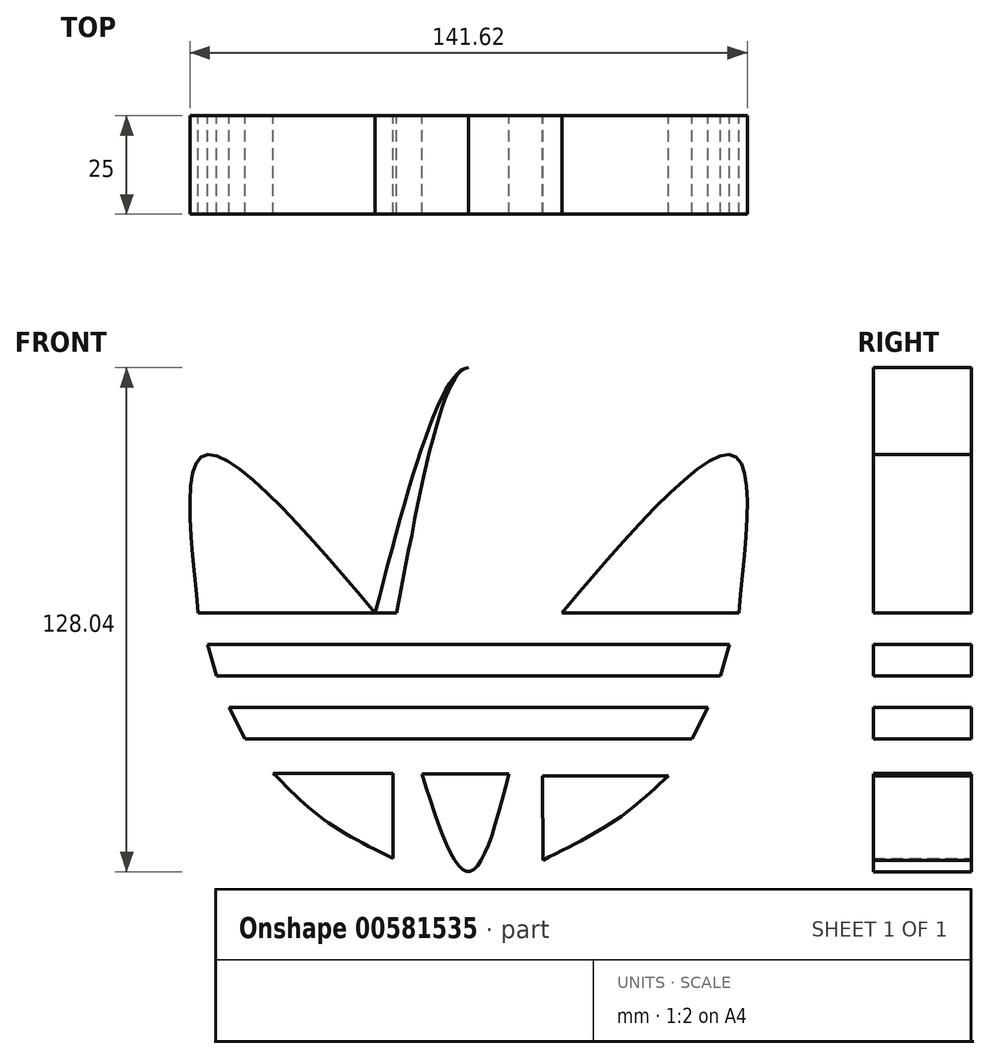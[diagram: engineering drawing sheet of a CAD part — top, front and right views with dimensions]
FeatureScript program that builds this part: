
annotation { "Feature Type Name" : "Feature", "Feature Type Description" : "" }
export const myFeature = defineFeature(function(context is Context, id is Id, definition is map)
    precondition{}
    {
        {
            var Q0;
            Q0=qCreatedBy(makeId("Front.planeOp"),FACE);
            var sketch = newSketch(context, id + "F0", { "sketchPlane" : qUnion([Q0])});
            skPoint(sketch, "E0", {"position": v(-0.15, -17.66) * mm});
            skLineSegment(sketch, "E1", {"start": v(-23.7, 0) * mm, "end": v(-68.7, 0) * mm});
            skFitSpline(sketch, "E2", {"points": [v(-23.7, 0) * mm, v(-67.37, 40) * mm, v(-68.7, 0) * mm], "startDerivative": vector(-83.92, 99.82) * mm, "endDerivative": vector(8.52, -106.38) * mm});
            skLineSegment(sketch, "E3", {"start": v(-23.7, 0) * mm, "end": v(0, 0) * mm});
            skFitSpline(sketch, "E4", {"points": [v(-23.7, 0) * mm, v(0, 62.34) * mm, v(18.3, 0) * mm], "startDerivative": vector(47.26, 186.76) * mm, "endDerivative": vector(36.72, -187.32) * mm});
            skLineSegment(sketch, "E5", {"start": v(-66.3, -8) * mm, "end": v(0, -8) * mm});
            skLineSegment(sketch, "E6", {"start": v(0, -16) * mm, "end": v(-63.96, -16) * mm});
            skLineSegment(sketch, "E7", {"start": v(-63.96, -16) * mm, "end": v(-66.3, -8) * mm});
            skLineSegment(sketch, "E8", {"start": v(-60.81, -24) * mm, "end": v(0, -24) * mm});
            skLineSegment(sketch, "E9", {"start": v(0, -32) * mm, "end": v(-56.77, -32) * mm});
            skLineSegment(sketch, "E10", {"start": v(-49.6, -40.67) * mm, "end": v(-19.16, -40.67) * mm});
            skLineSegment(sketch, "E11", {"start": v(-19.16, -40.67) * mm, "end": v(-19.16, -62.32) * mm});
            skLineSegment(sketch, "E12", {"start": v(-60.81, -24) * mm, "end": v(-56.77, -32) * mm});
            skPoint(sketch, "E13.1.internal.orphan", {"position": v(67.73, 40) * mm});
            skPoint(sketch, "E14.end.orphan", {"position": v(50.75, -41.32) * mm});
            skPoint(sketch, "E15.start.orphan", {"position": v(18.3, -40.67) * mm});
            skFitSpline(sketch, "E16.MirrorCS", {"points": [v(23.7, 0) * mm, v(0, 62.34) * mm, v(-18.3, 0) * mm], "startDerivative": vector(-47.26, 186.76) * mm, "endDerivative": vector(-36.72, -187.32) * mm});
            skFitSpline(sketch, "E17.MirrorCS", {"points": [v(23.7, 0) * mm, v(67.37, 40) * mm, v(68.7, 0) * mm], "startDerivative": vector(83.92, 99.82) * mm, "endDerivative": vector(-8.52, -106.38) * mm});
            skLineSegment(sketch, "E18.MirrorCS", {"start": v(23.7, 0) * mm, "end": v(68.7, 0) * mm});
            skLineSegment(sketch, "E19.MirrorCS", {"start": v(66.3, -8) * mm, "end": v(0, -8) * mm});
            skLineSegment(sketch, "E20.MirrorCS", {"start": v(63.96, -16) * mm, "end": v(66.3, -8) * mm});
            skLineSegment(sketch, "E21.MirrorCS", {"start": v(0, -16) * mm, "end": v(63.96, -16) * mm});
            skLineSegment(sketch, "E22.MirrorCS", {"start": v(60.81, -24) * mm, "end": v(0, -24) * mm});
            skLineSegment(sketch, "E23.MirrorCS", {"start": v(0, -32) * mm, "end": v(56.77, -32) * mm});
            skLineSegment(sketch, "E24.MirrorCS", {"start": v(60.81, -24) * mm, "end": v(56.77, -32) * mm});
            skLineSegment(sketch, "E25.MirrorCS", {"start": v(50.75, -41.32) * mm, "end": v(18.75, -41.32) * mm});
            skLineSegment(sketch, "E26.MirrorCS", {"start": v(18.75, -41.32) * mm, "end": v(18.86, -62.78) * mm});
            skLineSegment(sketch, "E27", {"start": v(-11.83, -40.82) * mm, "end": v(10.26, -40.82) * mm});
            skFitSpline(sketch, "E28", {"points": [v(-11.83, -40.82) * mm, v(0, -65.7) * mm, v(10.26, -40.82) * mm], "startDerivative": vector(24.26, -79.83) * mm, "endDerivative": vector(19.9, 80.1) * mm});
            skLineSegment(sketch, "E29", {"start": v(18.3, 0) * mm, "end": v(23.7, 0) * mm});
            skLineSegment(sketch, "E30", {"start": v(0, 0) * mm, "end": v(23.7, 0) * mm});
            skFitSpline(sketch, "E31", {"points": [v(-49.6, -40.67) * mm, v(-36.77, -52.46) * mm, v(-19.16, -62.32) * mm], "startDerivative": vector(24.93, -25.74) * mm, "endDerivative": vector(35.83, -17.67) * mm});
            skFitSpline(sketch, "E32", {"points": [v(50.75, -41.32) * mm, v(37.69, -52.39) * mm, v(18.86, -62.78) * mm], "startDerivative": vector(-25.87, -24.33) * mm, "endDerivative": vector(-37.7, -18.68) * mm});
            skSolve(sketch);
        }
        {
            var Q0;
            Q0=makeQuery(id+"F0.imprint","IMPRINT",FACE,{"disambiguationData":[TD([[makeQuery(id+"F0.imprint","IMPRINT",EDGE,{"derivedFrom":sQuery(id+"F0.wireOp",EDGE,"E1")}),-1.0]])]});
            var Q1;
            {var subQ0=sQuery(id+"F0.wireOp",EDGE,"E3");Q1=makeQuery(id+"F0.imprint","IMPRINT",FACE,{"disambiguationData":[TD([[makeQuery(id+"F0.imprint","IMPRINT",EDGE,{"derivedFrom":subQ0}),1.0]])]});}
            var Q2;
            Q2=makeQuery(id+"F0.imprint","IMPRINT",FACE,{"disambiguationData":[TD([[makeQuery(id+"F0.imprint","IMPRINT",EDGE,{"derivedFrom":sQuery(id+"F0.wireOp",EDGE,"E17.MirrorCS")}),-1.0]])]});
            var Q3;
            Q3=makeQuery(id+"F0.imprint","IMPRINT",FACE,{"disambiguationData":[TD([[makeQuery(id+"F0.imprint","IMPRINT",EDGE,{"derivedFrom":sQuery(id+"F0.wireOp",EDGE,"E5")}),-1.0]])]});
            var Q4;
            Q4=makeQuery(id+"F0.imprint","IMPRINT",FACE,{"disambiguationData":[TD([[makeQuery(id+"F0.imprint","IMPRINT",EDGE,{"derivedFrom":sQuery(id+"F0.wireOp",EDGE,"E8")}),-1.0]])]});
            var Q5;
            Q5=makeQuery(id+"F0.imprint","IMPRINT",FACE,{"disambiguationData":[TD([[makeQuery(id+"F0.imprint","IMPRINT",EDGE,{"derivedFrom":sQuery(id+"F0.wireOp",EDGE,"E25.MirrorCS")}),1.0]])]});
            var Q6;
            Q6=makeQuery(id+"F0.imprint","IMPRINT",FACE,{"disambiguationData":[TD([[makeQuery(id+"F0.imprint","IMPRINT",EDGE,{"derivedFrom":sQuery(id+"F0.wireOp",EDGE,"E27")}),-1.0]])]});
            var Q7;
            Q7=makeQuery(id+"F0.imprint","IMPRINT",FACE,{"disambiguationData":[TD([[makeQuery(id+"F0.imprint","IMPRINT",EDGE,{"derivedFrom":sQuery(id+"F0.wireOp",EDGE,"E10")}),-1.0]])]});
            extrude(context, id + "F1", {"entities" : qUnion([Q0, Q1, Q2, Q3, Q4, Q5, Q6, Q7]), "depth" : 25 * mm, "offsetDistance" : 25 * mm});
        }
    });
